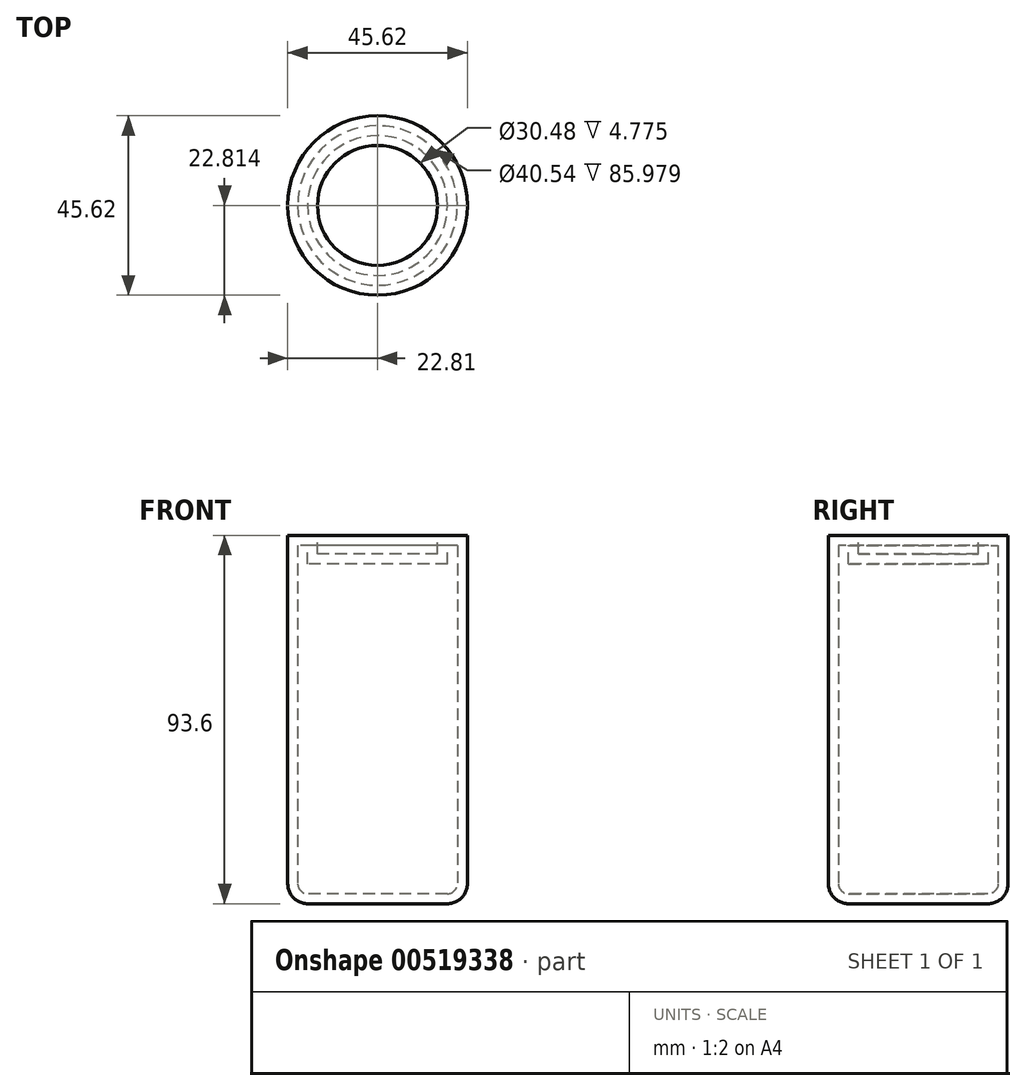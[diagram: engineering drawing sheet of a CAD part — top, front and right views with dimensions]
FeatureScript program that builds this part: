
annotation { "Feature Type Name" : "Feature", "Feature Type Description" : "" }
export const myFeature = defineFeature(function(context is Context, id is Id, definition is map)
    precondition{}
    {
        {
            var Q0;
            Q0=qCreatedBy(makeId("Top.planeOp"),FACE);
            var sketch = newSketch(context, id + "F0", { "sketchPlane" : qUnion([Q0])});
            skCircle(sketch, "E0", {"center": v(-112.98, -38.88) * mm, "radius": 22.8 * mm});
            skSolve(sketch);
        }
        {
            var Q0;
            Q0 = qSketchRegion(id + "F0", true);
            extrude(context, id + "F1", {"entities" : qUnion([Q0]), "depth" : 93.6 * mm, "offsetDistance" : 25.4 * mm});
        }
        {
            var Q0;
            Q0=makeQuery(id+"F1.opExtrude","CAP_FACE",FACE,{"disambiguationData":[OSD([sQuery(id+"F0.wireOp",EDGE,"E0")])],"isStart":false});
            var sketch = newSketch(context, id + "F2", { "sketchPlane" : qUnion([Q0])});
            skCircle(sketch, "E1", {"center": v(-112.98, -38.88) * mm, "radius": 15.24 * mm});
            skSolve(sketch);
        }
        {
            var Q0;
            Q0=makeQuery(id+"F2.imprint","IMPRINT",FACE,{"disambiguationData":[TD([[makeQuery(id+"F2.imprint","IMPRINT",EDGE,{"derivedFrom":sQuery(id+"F2.wireOp",EDGE,"E1")}),1.0]])]});
            extrude(context, id + "F3", {"entities" : qUnion([Q0]), "operationType" : NewBodyOperationType.REMOVE, "oppositeDirection" : true, "depth" : 4.78 * mm, "offsetDistance" : 25.4 * mm});
        }
        {
            var Q0;
            Q0=makeQuery(id+"F1.opExtrude","CAP_EDGE",EDGE,{"disambiguationData":[OSD([sQuery(id+"F0.wireOp",EDGE,"E0")])],"isStart":true});
            fillet(context, id + "F4", {"entities" : qUnion([Q0]), "radius" : 5.08 * mm, "tangentPropagation" : true, "allowEdgeOverflow" : false});
        }
        {
            var Q0;
            Q0=makeQuery(id+"F1.opExtrude","SWEPT_FACE",FACE,{"disambiguationData":[OSD([sQuery(id+"F0.wireOp",EDGE,"E0")])]});
            var Q1;
            Q1=makeQuery(id+"F3.boolean.opBoolean","COPY",FACE,{"derivedFrom":makeQuery(id+"F3.opExtrude","CAP_FACE",FACE,{"disambiguationData":[OSD([sQuery(id+"F2.wireOp",EDGE,"E1")])],"isStart":false})});
            var Q2;
            Q2=makeQuery(id+"F3.boolean.opBoolean","COPY",FACE,{"derivedFrom":makeQuery(id+"F3.opExtrude","SWEPT_FACE",FACE,{"disambiguationData":[OSD([sQuery(id+"F2.wireOp",EDGE,"E1")])]})});
            var Q3;
            Q3=makeQuery(id+"F1.opExtrude","SWEPT_BODY",BODY,{"disambiguationData":[OSD([sQuery(id+"F0.wireOp",EDGE,"E0")])]});
            shell(context, id + "F5", {"isHollow" : true, "entities" : qUnion([Q0, Q1, Q2]), "parts" : qUnion([Q3]), "thickness" : 2.54 * mm});
        }
    });
